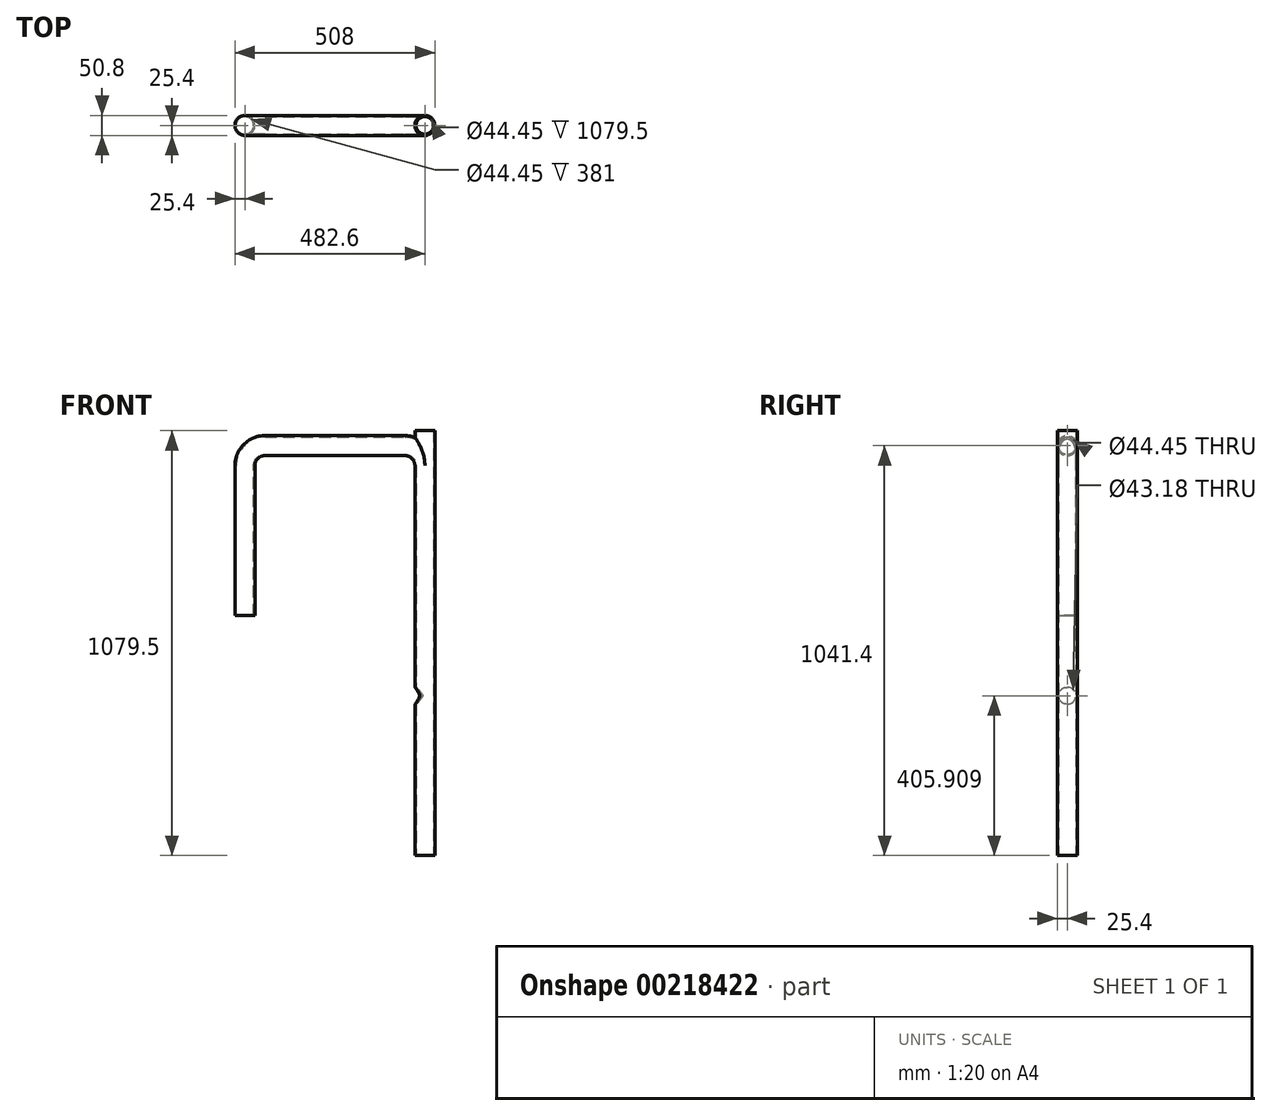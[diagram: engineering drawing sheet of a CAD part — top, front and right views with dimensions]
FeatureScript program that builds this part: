
annotation { "Feature Type Name" : "Feature", "Feature Type Description" : "" }
export const myFeature = defineFeature(function(context is Context, id is Id, definition is map)
    precondition{}
    {
        {
            var Q0;
            Q0=qCreatedBy(makeId("Front.planeOp"),FACE);
            var sketch = newSketch(context, id + "F0", { "sketchPlane" : qUnion([Q0])});
            skLineSegment(sketch, "E0", {"start": v(-50.8, -381) * mm, "end": v(-50.8, 0) * mm});
            skLineSegment(sketch, "E1", {"start": v(0, 50.8) * mm, "end": v(355.6, 50.8) * mm});
            skLineSegment(sketch, "E2", {"start": v(406.4, 0) * mm, "end": v(406.4, -990.6) * mm});
            skPoint(sketch, "E3.visualSharp", {"position": v(-50.8, 50.8) * mm});
            skArc(sketch, "E3.filletArc", {"start": v(0, 50.8) * mm, "mid": v(-35.92, 35.92) * mm, "end": v(-50.8, 0) * mm});
            skPoint(sketch, "E4.visualSharp", {"position": v(406.4, 50.8) * mm});
            skArc(sketch, "E4.filletArc", {"start": v(406.4, 0) * mm, "mid": v(391.52, 35.92) * mm, "end": v(355.6, 50.8) * mm});
            skSolve(sketch);
        }
        {
            var Q0;
            Q0=qCreatedBy(makeId("Top.planeOp"),FACE);
            cPlane(context, id + "F1", {"entities" : qUnion([Q0]), "cplaneType" : CPlaneType.OFFSET, "offset" : 381 * mm, "oppositeDirection" : true, "width" : 152.4 * mm, "height" : 152.4 * mm});
        }
        {
            var Q0;
            Q0=qCreatedBy(id+"F1.planeOp",FACE);
            var sketch = newSketch(context, id + "F2", { "sketchPlane" : qUnion([Q0])});
            skCircle(sketch, "E5", {"center": v(-50.8, 0) * mm, "radius": 25.4 * mm});
            skCircle(sketch, "E6", {"center": v(-50.8, 0) * mm, "radius": 22.23 * mm});
            skSolve(sketch);
        }
        {
            var Q0;
            Q0=makeQuery(id+"F2.imprint","IMPRINT",FACE,{"disambiguationData":[TD([[makeQuery(id+"F2.imprint","IMPRINT",EDGE,{"derivedFrom":sQuery(id+"F2.wireOp",EDGE,"E5")}),1.0]])]});
            var Q1;
            Q1=sQuery(id+"F0.wireOp",EDGE,"E0");
            var Q2;
            Q2=sQuery(id+"F0.wireOp",EDGE,"E3.filletArc");
            var Q3;
            Q3=sQuery(id+"F0.wireOp",EDGE,"E1");
            var Q4;
            Q4=sQuery(id+"F0.wireOp",EDGE,"E4.filletArc");
            var Q5;
            Q5=sQuery(id+"F0.wireOp",EDGE,"E2");
            sweep(context, id + "F3", {"profiles" : qUnion([Q0]), "path" : qUnion([Q1, Q2, Q3, Q4, Q5])});
        }
        {
            var Q0;
            Q0=qCreatedBy(makeId("Top.planeOp"),FACE);
            cPlane(context, id + "F4", {"entities" : qUnion([Q0]), "cplaneType" : CPlaneType.OFFSET, "offset" : 88.9 * mm, "width" : 152.4 * mm, "height" : 152.4 * mm});
        }
        {
            var Q0;
            Q0=qCreatedBy(id+"F4.planeOp",FACE);
            var sketch = newSketch(context, id + "F5", { "sketchPlane" : qUnion([Q0])});
            skCircle(sketch, "E7", {"center": v(406.4, 0) * mm, "radius": 25.4 * mm});
            skCircle(sketch, "E8", {"center": v(406.4, 0) * mm, "radius": 22.23 * mm});
            skSolve(sketch);
        }
        {
            var Q0;
            Q0=makeQuery(id+"F5.imprint","IMPRINT",FACE,{"disambiguationData":[TD([[makeQuery(id+"F5.imprint","IMPRINT",EDGE,{"derivedFrom":sQuery(id+"F5.wireOp",EDGE,"E7")}),1.0]])]});
            var Q1;
            Q1=makeQuery(id+"F3.opSweep","SWEPT_BODY",BODY,{"disambiguationData":[OSD([sQuery(id+"F0.wireOp",EDGE,"E2"),sQuery(id+"F2.wireOp",EDGE,"E5"),sQuery(id+"F2.wireOp",EDGE,"E6")])]});
            extrude(context, id + "F6", {"entities" : qUnion([Q0]), "operationType" : NewBodyOperationType.ADD, "endBound" : BoundingType.UP_TO_BODY, "oppositeDirection" : true, "endBoundEntityBody" : qUnion([Q1]), "depth" : 25.4 * mm});
        }
        {
            var Q0;
            Q0=qCreatedBy(id+"F4.planeOp",FACE);
            var sketch = newSketch(context, id + "F7", { "sketchPlane" : qUnion([Q0])});
            skCircle(sketch, "E9", {"center": v(406.4, 0) * mm, "radius": 22.23 * mm});
            skSolve(sketch);
        }
        {
            var Q0;
            Q0 = qSketchRegion(id + "F7", true);
            extrude(context, id + "F8", {"entities" : qUnion([Q0]), "operationType" : NewBodyOperationType.REMOVE, "endBound" : BoundingType.THROUGH_ALL, "oppositeDirection" : true, "depth" : 25.4 * mm});
        }
        {
            var Q0;
            Q0=qCreatedBy(makeId("Right.planeOp"),FACE);
            cPlane(context, id + "F9", {"entities" : qUnion([Q0]), "cplaneType" : CPlaneType.OFFSET, "offset" : 381 * mm, "width" : 152.4 * mm, "height" : 152.4 * mm});
        }
        {
            var Q0;
            Q0=qCreatedBy(id+"F9.planeOp",FACE);
            var sketch = newSketch(context, id + "F10", { "sketchPlane" : qUnion([Q0])});
            skCircle(sketch, "E10", {"center": v(0, -584.7) * mm, "radius": 21.59 * mm});
            skLineSegment(sketch, "E11", {"start": v(-24.79, -584.7) * mm, "end": v(26.01, -584.7) * mm, "construction": true});
            skSolve(sketch);
        }
        {
            var Q0;
            Q0=makeQuery(id+"F10.imprint","IMPRINT",FACE,{"disambiguationData":[TD([[makeQuery(id+"F10.imprint","IMPRINT",EDGE,{"derivedFrom":sQuery(id+"F10.wireOp",EDGE,"E10")}),1.0]])]});
            extrude(context, id + "F11", {"entities" : qUnion([Q0]), "operationType" : NewBodyOperationType.REMOVE, "depth" : 25.4 * mm});
        }
    });
